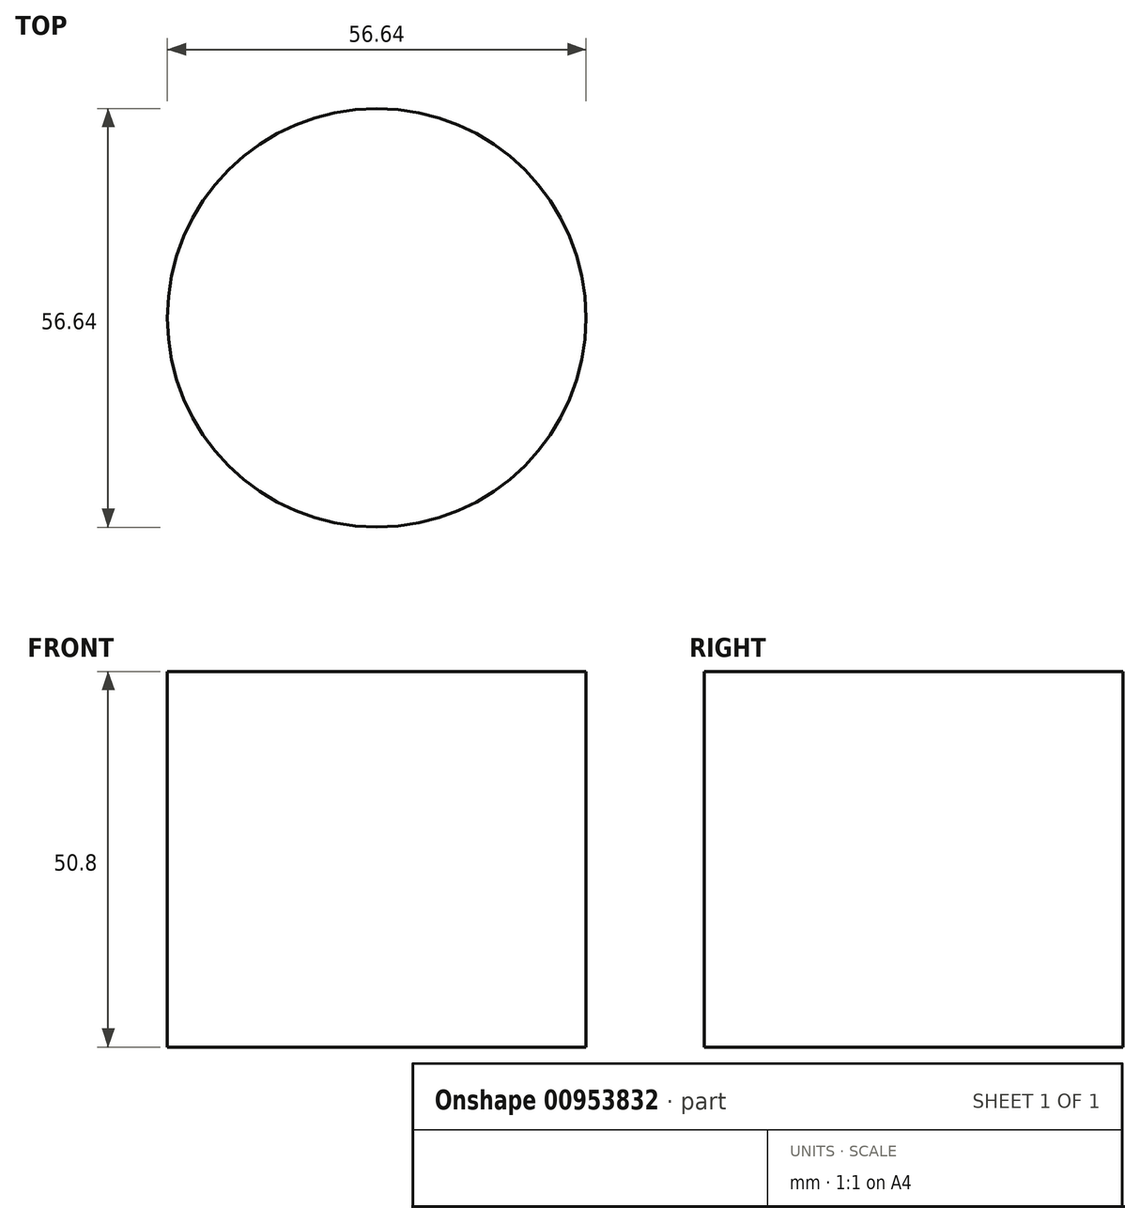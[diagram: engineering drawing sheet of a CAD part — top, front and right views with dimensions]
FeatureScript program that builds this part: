
annotation { "Feature Type Name" : "Feature", "Feature Type Description" : "" }
export const myFeature = defineFeature(function(context is Context, id is Id, definition is map)
    precondition{}
    {
        {
            var Q0;
            Q0=qCreatedBy(makeId("Top.planeOp"),FACE);
            var sketch = newSketch(context, id + "F0", { "sketchPlane" : qUnion([Q0])});
            skCircle(sketch, "E0", {"center": v(0, 0) * mm, "radius": 28.32 * mm});
            skSolve(sketch);
        }
        {
            var Q0;
            Q0=makeQuery(id+"F0.imprint","IMPRINT",FACE,{"disambiguationData":[TD([[makeQuery(id+"F0.imprint","IMPRINT",EDGE,{"derivedFrom":sQuery(id+"F0.wireOp",EDGE,"E0")}),1.0]])]});
            extrude(context, id + "F1", {"entities" : qUnion([Q0]), "depth" : 50.8 * mm, "offsetDistance" : 25.4 * mm});
        }
    });
